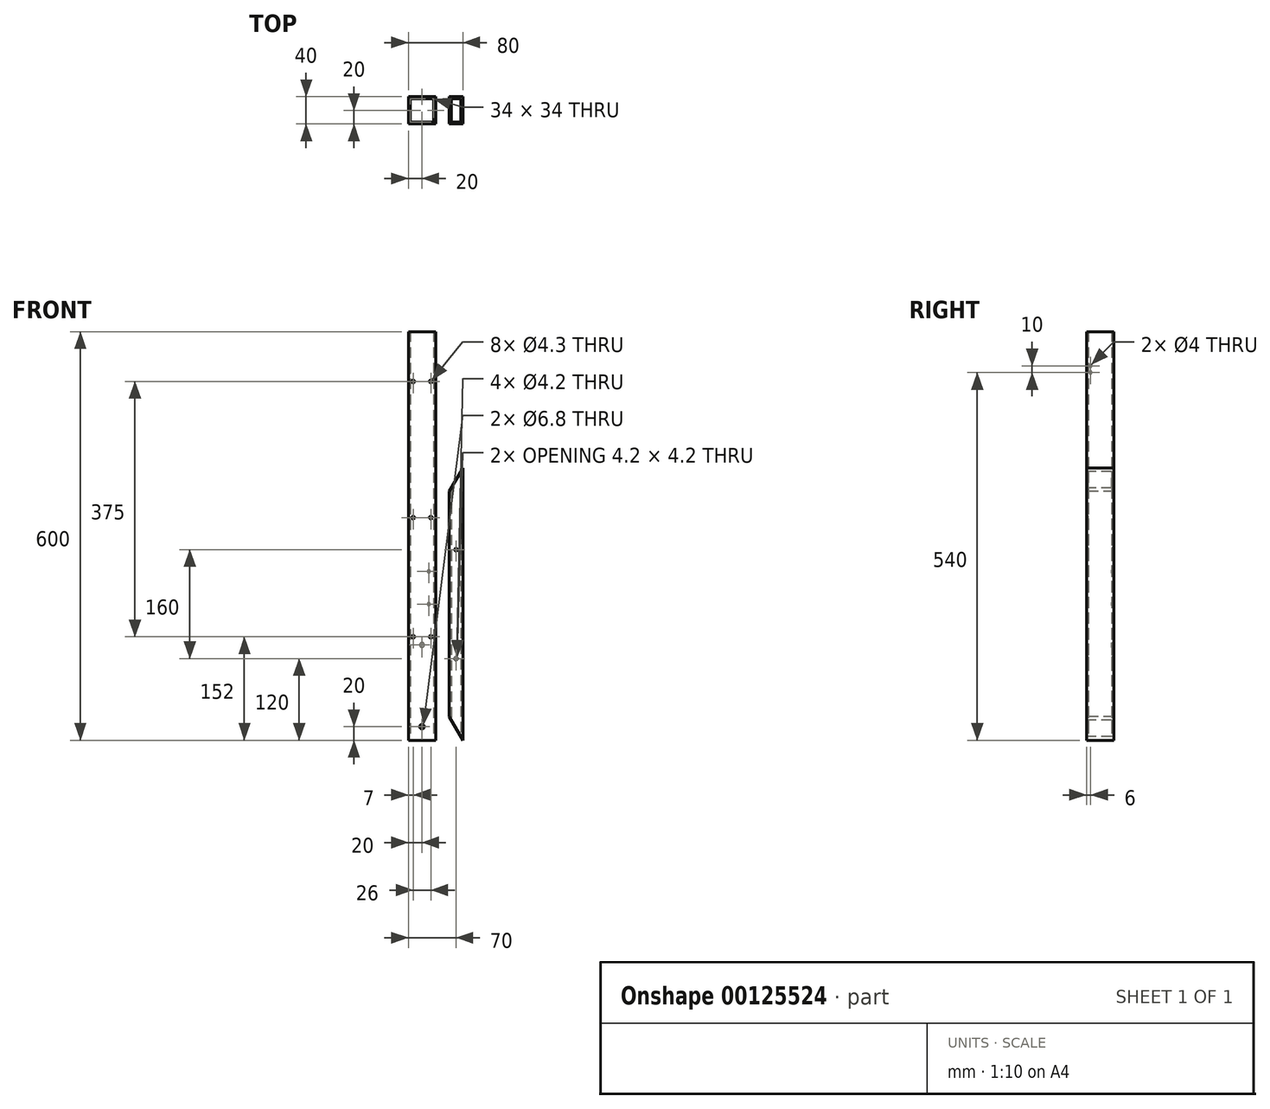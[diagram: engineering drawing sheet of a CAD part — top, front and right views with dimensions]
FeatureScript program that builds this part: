
annotation { "Feature Type Name" : "Feature", "Feature Type Description" : "" }
export const myFeature = defineFeature(function(context is Context, id is Id, definition is map)
    precondition{}
    {
        {
            var Q0;
            Q0=qCreatedBy(makeId("Top.planeOp"),FACE);
            var sketch = newSketch(context, id + "F0", { "sketchPlane" : qUnion([Q0])});
            skLineSegment(sketch, "E0.bottom", {"start": v(-10, 20) * mm, "end": v(-50, 20) * mm});
            skLineSegment(sketch, "E0.top", {"start": v(-10, -20) * mm, "end": v(-50, -20) * mm});
            skLineSegment(sketch, "E0.left", {"start": v(-10, 20) * mm, "end": v(-10, -20) * mm});
            skLineSegment(sketch, "E0.right", {"start": v(-50, 20) * mm, "end": v(-50, -20) * mm});
            skPoint(sketch, "E0.middle", {"position": v(-30, 0) * mm});
            skLineSegment(sketch, "E1.bottom", {"start": v(30, 20) * mm, "end": v(10, 20) * mm});
            skLineSegment(sketch, "E1.top", {"start": v(30, -20) * mm, "end": v(10, -20) * mm});
            skLineSegment(sketch, "E1.left", {"start": v(30, 20) * mm, "end": v(30, -20) * mm});
            skLineSegment(sketch, "E1.right", {"start": v(10, 20) * mm, "end": v(10, -20) * mm});
            skPoint(sketch, "E1.middle", {"position": v(20, 0) * mm});
            skLineSegment(sketch, "E2.bottom", {"start": v(-13, 17) * mm, "end": v(-47, 17) * mm});
            skLineSegment(sketch, "E2.top", {"start": v(-13, -17) * mm, "end": v(-47, -17) * mm});
            skLineSegment(sketch, "E2.left", {"start": v(-13, 17) * mm, "end": v(-13, -17) * mm});
            skLineSegment(sketch, "E2.right", {"start": v(-47, 17) * mm, "end": v(-47, -17) * mm});
            skLineSegment(sketch, "E3.bottom", {"start": v(13, 17) * mm, "end": v(27, 17) * mm});
            skLineSegment(sketch, "E3.top", {"start": v(13, -17) * mm, "end": v(27, -17) * mm});
            skLineSegment(sketch, "E3.left", {"start": v(13, 17) * mm, "end": v(13, -17) * mm});
            skLineSegment(sketch, "E3.right", {"start": v(27, 17) * mm, "end": v(27, -17) * mm});
            skSolve(sketch);
        }
        {
            var Q0;
            Q0=makeQuery(id+"F0.imprint","IMPRINT",FACE,{"disambiguationData":[TD([[makeQuery(id+"F0.imprint","IMPRINT",EDGE,{"derivedFrom":sQuery(id+"F0.wireOp",EDGE,"E0.bottom")}),1.0]])]});
            extrude(context, id + "F1", {"entities" : qUnion([Q0]), "depth" : 600 * mm});
        }
        {
            var Q0;
            Q0=makeQuery(id+"F0.imprint","IMPRINT",FACE,{"disambiguationData":[TD([[makeQuery(id+"F0.imprint","IMPRINT",EDGE,{"derivedFrom":sQuery(id+"F0.wireOp",EDGE,"E1.bottom")}),1.0]])]});
            extrude(context, id + "F2", {"entities" : qUnion([Q0]), "depth" : 400 * mm});
        }
        {
            var Q0;
            Q0=makeQuery(id+"F2.opExtrude","SWEPT_FACE",FACE,{"disambiguationData":[OSD([sQuery(id+"F0.wireOp",EDGE,"E1.top")])]});
            var sketch = newSketch(context, id + "F3", { "sketchPlane" : qUnion([Q0])});
            skLineSegment(sketch, "E4", {"start": v(30, 0) * mm, "end": v(10, 34.64) * mm});
            skLineSegment(sketch, "E5", {"start": v(30, 400) * mm, "end": v(10, 365.36) * mm});
            skSolve(sketch);
        }
        {
            var Q0;
            {var subQ0=sQuery(id+"F3.wireOp",EDGE,"E5");Q0=makeQuery(id+"F3.imprint","IMPRINT",FACE,{"disambiguationData":[TD([[makeQuery(id+"F3.imprint","IMPRINT",EDGE,{"derivedFrom":subQ0}),-1.0]])]});}
            var Q1;
            {var subQ0=sQuery(id+"F3.wireOp",EDGE,"E4");Q1=makeQuery(id+"F3.imprint","IMPRINT",FACE,{"disambiguationData":[TD([[makeQuery(id+"F3.imprint","IMPRINT",EDGE,{"derivedFrom":subQ0}),1.0]])]});}
            extrude(context, id + "F4", {"entities" : qUnion([Q0, Q1]), "operationType" : NewBodyOperationType.REMOVE, "endBound" : BoundingType.THROUGH_ALL, "oppositeDirection" : true, "depth" : 25 * mm});
        }
        {
            var Q0;
            Q0=makeQuery(id+"F1.opExtrude","SWEPT_FACE",FACE,{"disambiguationData":[OSD([sQuery(id+"F0.wireOp",EDGE,"E0.top")])]});
            var sketch = newSketch(context, id + "F5", { "sketchPlane" : qUnion([Q0])});
            skCircle(sketch, "E6", {"center": v(-43, 527) * mm, "radius": 2.15 * mm});
            skCircle(sketch, "E7", {"center": v(-17, 527) * mm, "radius": 2.15 * mm});
            skPoint(sketch, "E8", {"position": v(-30, 600) * mm});
            skCircle(sketch, "E9", {"center": v(-43, 327) * mm, "radius": 2.15 * mm});
            skCircle(sketch, "E10", {"center": v(-17, 327) * mm, "radius": 2.15 * mm});
            skCircle(sketch, "E11", {"center": v(-43, 152) * mm, "radius": 2.15 * mm});
            skCircle(sketch, "E12", {"center": v(-17, 152) * mm, "radius": 2.15 * mm});
            skLineSegment(sketch, "E13", {"start": v(-43, 527) * mm, "end": v(-43, 327) * mm, "construction": true});
            skLineSegment(sketch, "E14", {"start": v(-43, 327) * mm, "end": v(-43, 152) * mm, "construction": true});
            skCircle(sketch, "E15", {"center": v(-30, 20) * mm, "radius": 3.4 * mm});
            skPoint(sketch, "E15.centerSnap0", {"position": v(-30, 0) * mm});
            skSolve(sketch);
        }
        {
            var Q0;
            Q0 = qSketchRegion(id + "F5", true);
            extrude(context, id + "F6", {"entities" : qUnion([Q0]), "operationType" : NewBodyOperationType.REMOVE, "oppositeDirection" : true, "depth" : 25 * mm});
        }
        {
            var Q0;
            Q0=makeQuery(id+"F1.opExtrude","SWEPT_FACE",FACE,{"disambiguationData":[OSD([sQuery(id+"F0.wireOp",EDGE,"E0.right")])]});
            var sketch = newSketch(context, id + "F7", { "sketchPlane" : qUnion([Q0])});
            skCircle(sketch, "E16", {"center": v(14, 550) * mm, "radius": 2 * mm});
            skCircle(sketch, "E17", {"center": v(14, 540) * mm, "radius": 2 * mm});
            skSolve(sketch);
        }
        {
            var Q0;
            Q0=makeQuery(id+"F7.imprint","IMPRINT",FACE,{"disambiguationData":[TD([[makeQuery(id+"F7.imprint","IMPRINT",EDGE,{"derivedFrom":sQuery(id+"F7.wireOp",EDGE,"E16")}),1.0]])]});
            var Q1;
            Q1=makeQuery(id+"F7.imprint","IMPRINT",FACE,{"disambiguationData":[TD([[makeQuery(id+"F7.imprint","IMPRINT",EDGE,{"derivedFrom":sQuery(id+"F7.wireOp",EDGE,"E17")}),1.0]])]});
            extrude(context, id + "F8", {"entities" : qUnion([Q0, Q1]), "operationType" : NewBodyOperationType.REMOVE, "oppositeDirection" : true, "depth" : 25 * mm});
        }
        {
            var Q0;
            Q0=makeQuery(id+"F1.opExtrude","SWEPT_FACE",FACE,{"disambiguationData":[OSD([sQuery(id+"F0.wireOp",EDGE,"E0.bottom")])]});
            var sketch = newSketch(context, id + "F9", { "sketchPlane" : qUnion([Q0])});
            skCircle(sketch, "E18", {"center": v(30, 140) * mm, "radius": 3.4 * mm});
            skPoint(sketch, "E18.centerSnap0", {"position": v(30, 0) * mm});
            skCircle(sketch, "E19", {"center": v(20, 200) * mm, "radius": 2.15 * mm});
            skCircle(sketch, "E20", {"center": v(20, 248) * mm, "radius": 2.15 * mm});
            skSolve(sketch);
        }
        {
            var Q0;
            Q0=makeQuery(id+"F9.imprint","IMPRINT",FACE,{"disambiguationData":[TD([[makeQuery(id+"F9.imprint","IMPRINT",EDGE,{"derivedFrom":sQuery(id+"F9.wireOp",EDGE,"E18")}),1.0]])]});
            var Q1;
            Q1=makeQuery(id+"F9.imprint","IMPRINT",FACE,{"disambiguationData":[TD([[makeQuery(id+"F9.imprint","IMPRINT",EDGE,{"derivedFrom":sQuery(id+"F9.wireOp",EDGE,"E19")}),1.0]])]});
            var Q2;
            Q2=makeQuery(id+"F9.imprint","IMPRINT",FACE,{"disambiguationData":[TD([[makeQuery(id+"F9.imprint","IMPRINT",EDGE,{"derivedFrom":sQuery(id+"F9.wireOp",EDGE,"E20")}),1.0]])]});
            extrude(context, id + "F10", {"entities" : qUnion([Q0, Q1, Q2]), "operationType" : NewBodyOperationType.REMOVE, "oppositeDirection" : true, "depth" : 25 * mm});
        }
        {
            var Q0;
            Q0=makeQuery(id+"F2.opExtrude","SWEPT_FACE",FACE,{"disambiguationData":[OSD([sQuery(id+"F0.wireOp",EDGE,"E1.top")])]});
            var sketch = newSketch(context, id + "F11", { "sketchPlane" : qUnion([Q0])});
            skCircle(sketch, "E21", {"center": v(20, 280) * mm, "radius": 2.1 * mm});
            skCircle(sketch, "E22", {"center": v(20, 120) * mm, "radius": 2.1 * mm});
            skPoint(sketch, "E23", {"position": v(10, 200) * mm});
            skSolve(sketch);
        }
        {
            var Q0;
            Q0 = qSketchRegion(id + "F11", true);
            extrude(context, id + "F12", {"entities" : qUnion([Q0]), "operationType" : NewBodyOperationType.REMOVE, "endBound" : BoundingType.THROUGH_ALL, "oppositeDirection" : true, "depth" : 25 * mm});
        }
    });
